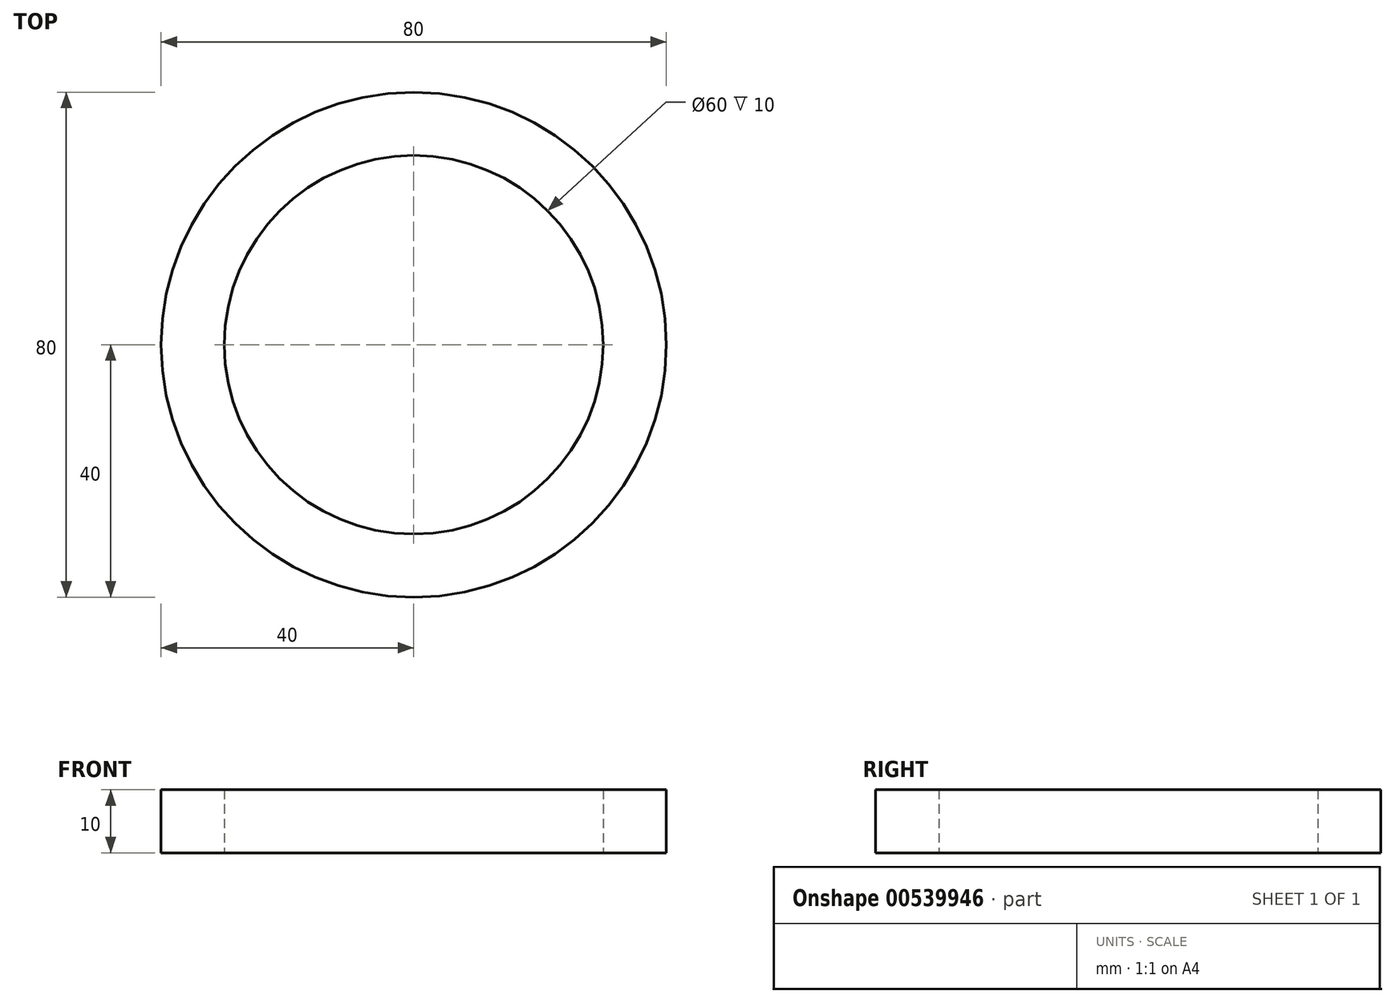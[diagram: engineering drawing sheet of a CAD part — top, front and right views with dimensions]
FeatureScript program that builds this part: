
annotation { "Feature Type Name" : "Feature", "Feature Type Description" : "" }
export const myFeature = defineFeature(function(context is Context, id is Id, definition is map)
    precondition{}
    {
        {
            var Q0;
            Q0=qCreatedBy(makeId("Front.planeOp"),FACE);
            var sketch = newSketch(context, id + "F0", { "sketchPlane" : qUnion([Q0])});
            skLineSegment(sketch, "E0.bottom", {"start": v(-30, -5) * mm, "end": v(-40, -5) * mm});
            skLineSegment(sketch, "E0.top", {"start": v(-30, 5) * mm, "end": v(-40, 5) * mm});
            skLineSegment(sketch, "E0.left", {"start": v(-30, -5) * mm, "end": v(-30, 5) * mm});
            skLineSegment(sketch, "E0.right", {"start": v(-40, -5) * mm, "end": v(-40, 5) * mm});
            skSolve(sketch);
        }
        {
            var Q0;
            Q0=qCreatedBy(makeId("Front.planeOp"),FACE);
            var sketch = newSketch(context, id + "F1", { "sketchPlane" : qUnion([Q0])});
            skLineSegment(sketch, "E1", {"start": v(0, -28.1) * mm, "end": v(0, 49.62) * mm, "construction": true});
            skLineSegment(sketch, "E2", {"start": v(0, 49.62) * mm, "end": v(0, 24.69) * mm, "construction": true});
            skSolve(sketch);
        }
        {
            var Q0;
            Q0=makeQuery(id+"F0.imprint","IMPRINT",FACE,{"disambiguationData":[TD([[makeQuery(id+"F0.imprint","IMPRINT",EDGE,{"derivedFrom":sQuery(id+"F0.wireOp",EDGE,"E0.bottom")}),-1.0]])]});
            var Q1;
            Q1=sQuery(id+"F1.wireOp",EDGE,"E1");
            revolve(context, id + "F2", {"entities" : qUnion([Q0]), "axis" : qUnion([Q1]), "revolveType" : RevolveType.FULL});
        }
    });
